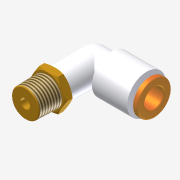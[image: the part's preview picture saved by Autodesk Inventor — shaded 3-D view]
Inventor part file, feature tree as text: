
AUTODESK INVENTOR PART (.ipt)
format: ipt  version: unknown  size: 250,368 bytes
history: native  units: mm
features: imported_body x1, thread x1
ambient origin geometry x8: Origin, YZ Plane, XZ Plane, XY Plane, X Axis, Y Axis, Z Axis, Center Point
feature tree (2):
  imported_body  "Base1"
  thread  "Thread1"  [1 undecoded]
note: 1 required parameter value undecoded (feature->parameter linkage not recoverable at this tier; creation-order binding heuristic only, values carry confidence <= 0.55)
